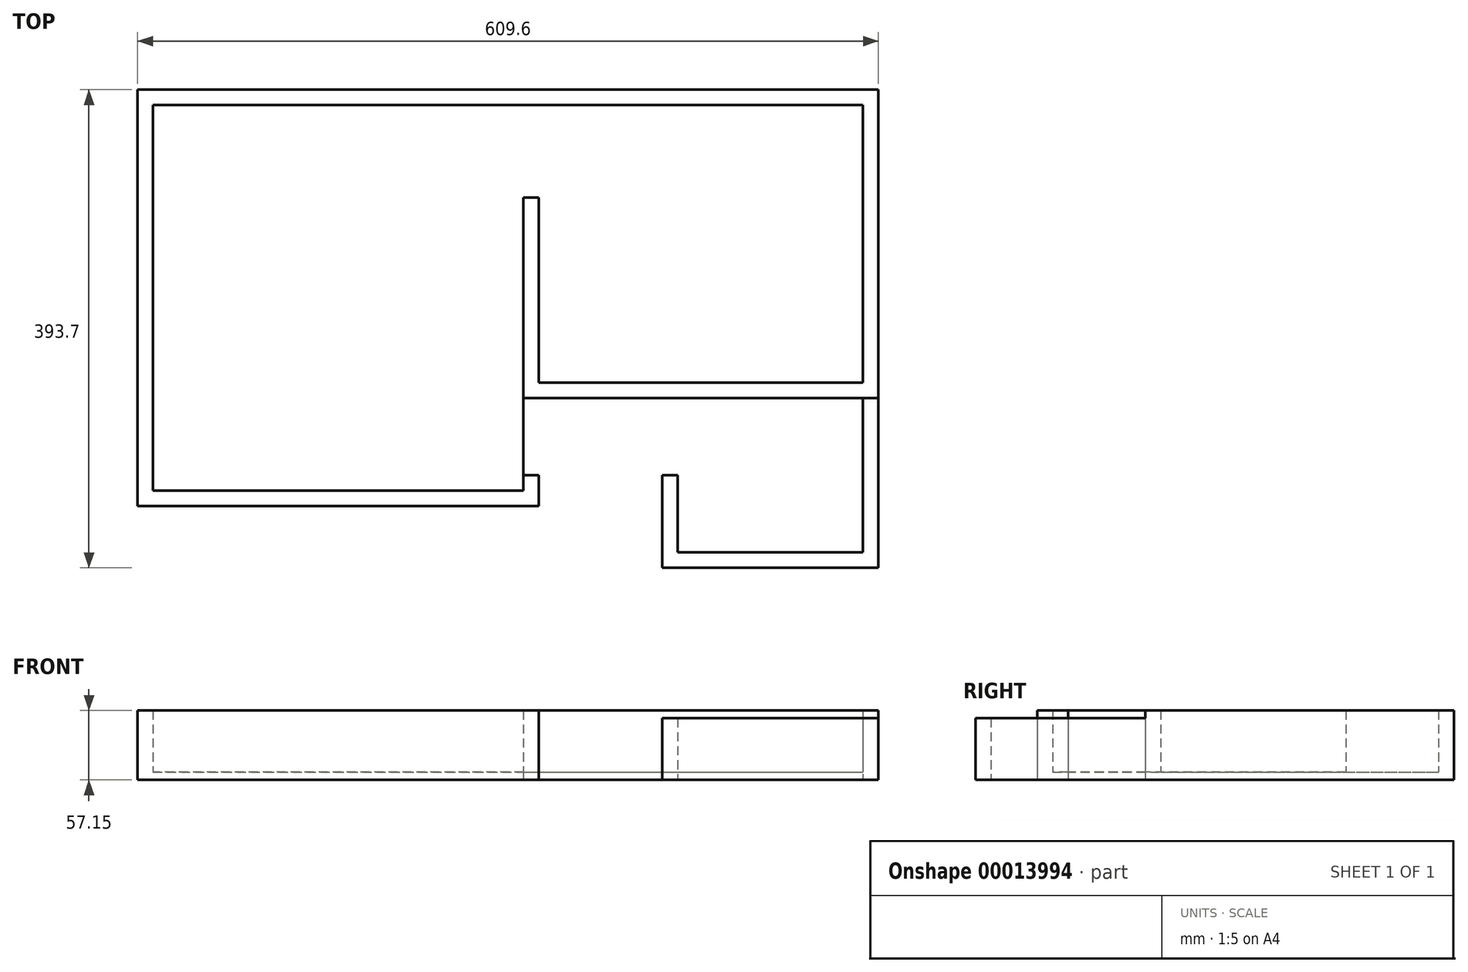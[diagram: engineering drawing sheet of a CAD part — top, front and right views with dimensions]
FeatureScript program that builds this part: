
annotation { "Feature Type Name" : "Feature", "Feature Type Description" : "" }
export const myFeature = defineFeature(function(context is Context, id is Id, definition is map)
    precondition{}
    {
        {
            var Q0;
            Q0=qCreatedBy(makeId("Top.planeOp"),FACE);
            var sketch = newSketch(context, id + "F0", { "sketchPlane" : qUnion([Q0])});
            skLineSegment(sketch, "E0", {"start": v(304.8, 0) * mm, "end": v(0, 0) * mm});
            skLineSegment(sketch, "E1", {"start": v(0, 0) * mm, "end": v(0, 317.5) * mm});
            skLineSegment(sketch, "E2", {"start": v(0, 317.5) * mm, "end": v(584.2, 317.5) * mm});
            skLineSegment(sketch, "E3", {"start": v(304.8, 88.9) * mm, "end": v(304.8, 0) * mm});
            skLineSegment(sketch, "E4", {"start": v(304.8, 88.9) * mm, "end": v(584.2, 88.9) * mm});
            skLineSegment(sketch, "E5", {"start": v(584.2, 88.9) * mm, "end": v(584.2, 317.5) * mm});
            skLineSegment(sketch, "E6.0", {"start": v(-12.7, 330.2) * mm, "end": v(596.9, 330.2) * mm});
            skLineSegment(sketch, "E6.1", {"start": v(-12.7, -12.7) * mm, "end": v(-12.7, 330.2) * mm});
            skLineSegment(sketch, "E6.2", {"start": v(317.5, -12.7) * mm, "end": v(-12.7, -12.7) * mm});
            skLineSegment(sketch, "E7.0", {"start": v(317.5, 76.2) * mm, "end": v(317.5, -12.7) * mm});
            skLineSegment(sketch, "E7.1", {"start": v(317.5, 76.2) * mm, "end": v(596.9, 76.2) * mm});
            skLineSegment(sketch, "E7.2", {"start": v(596.9, 76.2) * mm, "end": v(596.9, 330.2) * mm});
            skSolve(sketch);
        }
        {
            var Q0;
            Q0=makeQuery(id+"F0.imprint","IMPRINT",FACE,{"disambiguationData":[TD([[makeQuery(id+"F0.imprint","IMPRINT",EDGE,{"derivedFrom":sQuery(id+"F0.wireOp",EDGE,"E0")}),1.0]])]});
            extrude(context, id + "F1", {"entities" : qUnion([Q0]), "depth" : 50.8 * mm});
        }
        {
            var Q0;
            Q0=makeQuery(id+"F0.imprint","IMPRINT",FACE,{"disambiguationData":[TD([[makeQuery(id+"F0.imprint","IMPRINT",EDGE,{"derivedFrom":sQuery(id+"F0.wireOp",EDGE,"E0")}),-1.0]])]});
            var Q1;
            Q1=makeQuery(id+"F0.imprint","IMPRINT",FACE,{"disambiguationData":[TD([[makeQuery(id+"F0.imprint","IMPRINT",EDGE,{"derivedFrom":sQuery(id+"F0.wireOp",EDGE,"E0")}),1.0]])]});
            extrude(context, id + "F2", {"entities" : qUnion([Q0, Q1]), "operationType" : NewBodyOperationType.ADD, "oppositeDirection" : true, "depth" : 6.35 * mm});
        }
        {
            var Q0;
            Q0=makeQuery(id+"F2.opExtrude","CAP_FACE",FACE,{"disambiguationData":[OSD([sQuery(id+"F0.wireOp",EDGE,"E6.0"),sQuery(id+"F0.wireOp",EDGE,"E6.1"),sQuery(id+"F0.wireOp",EDGE,"E6.2"),sQuery(id+"F0.wireOp",EDGE,"E7.0"),sQuery(id+"F0.wireOp",EDGE,"E7.1"),sQuery(id+"F0.wireOp",EDGE,"E7.2")])],"isStart":true});
            var sketch = newSketch(context, id + "F3", { "sketchPlane" : qUnion([Q0])});
            skLineSegment(sketch, "E8", {"start": v(304.8, 241.3) * mm, "end": v(304.8, 88.9) * mm});
            skLineSegment(sketch, "E9", {"start": v(304.8, 241.3) * mm, "end": v(317.5, 241.3) * mm});
            skLineSegment(sketch, "E10", {"start": v(317.5, 241.3) * mm, "end": v(317.5, 88.9) * mm});
            skLineSegment(sketch, "E11", {"start": v(317.5, 88.9) * mm, "end": v(304.8, 88.9) * mm});
            skSolve(sketch);
        }
        {
            var Q0;
            Q0=makeQuery(id+"F3.imprint","IMPRINT",FACE,{"disambiguationData":[TD([[makeQuery(id+"F3.imprint","IMPRINT",EDGE,{"derivedFrom":sQuery(id+"F3.wireOp",EDGE,"E8")}),1.0]])]});
            extrude(context, id + "F4", {"entities" : qUnion([Q0]), "operationType" : NewBodyOperationType.ADD, "depth" : 50.8 * mm});
        }
        {
            var Q0;
            {var subQ0=sQuery(id+"F0.wireOp",EDGE,"E7.0");Q0=makeQuery(id+"F2.boolean.opBoolean","MERGE",FACE,{"derivedFrom":[makeQuery(id+"F1.opExtrude","SWEPT_FACE",FACE,{"disambiguationData":[OSD([subQ0])]}),makeQuery(id+"F2.opExtrude","SWEPT_FACE",FACE,{"disambiguationData":[OSD([subQ0])]})]});}
            var sketch = newSketch(context, id + "F5", { "sketchPlane" : qUnion([Q0])});
            skLineSegment(sketch, "E12", {"start": v(12.7, 50.8) * mm, "end": v(12.7, -6.35) * mm});
            skLineSegment(sketch, "E13", {"start": v(12.7, -6.35) * mm, "end": v(76.2, -6.35) * mm});
            skLineSegment(sketch, "E14", {"start": v(76.2, -6.35) * mm, "end": v(76.2, 50.8) * mm});
            skLineSegment(sketch, "E15", {"start": v(76.2, 50.8) * mm, "end": v(12.7, 50.8) * mm});
            skSolve(sketch);
        }
        {
            var Q0;
            Q0=makeQuery(id+"F2.opExtrude","CAP_FACE",FACE,{"disambiguationData":[OSD([sQuery(id+"F0.wireOp",EDGE,"E6.0"),sQuery(id+"F0.wireOp",EDGE,"E6.1"),sQuery(id+"F0.wireOp",EDGE,"E6.2"),sQuery(id+"F0.wireOp",EDGE,"E7.0"),sQuery(id+"F0.wireOp",EDGE,"E7.1"),sQuery(id+"F0.wireOp",EDGE,"E7.2")])],"isStart":false});
            var sketch = newSketch(context, id + "F6", { "sketchPlane" : qUnion([Q0])});
            skLineSegment(sketch, "E16", {"start": v(596.9, -76.2) * mm, "end": v(596.9, 63.5) * mm});
            skLineSegment(sketch, "E17", {"start": v(596.9, 63.5) * mm, "end": v(419.1, 63.5) * mm});
            skLineSegment(sketch, "E18", {"start": v(419.1, 63.5) * mm, "end": v(419.1, -12.7) * mm});
            skLineSegment(sketch, "E19", {"start": v(419.1, -12.7) * mm, "end": v(431.8, -12.7) * mm});
            skLineSegment(sketch, "E20", {"start": v(431.8, -12.7) * mm, "end": v(431.8, 50.8) * mm});
            skLineSegment(sketch, "E21", {"start": v(431.8, 50.8) * mm, "end": v(584.2, 50.8) * mm});
            skLineSegment(sketch, "E22", {"start": v(584.2, 50.8) * mm, "end": v(584.2, -76.2) * mm});
            skLineSegment(sketch, "E23", {"start": v(596.9, -76.2) * mm, "end": v(596.9, -88.9) * mm});
            skLineSegment(sketch, "E24", {"start": v(596.9, -88.9) * mm, "end": v(584.2, -88.9) * mm});
            skLineSegment(sketch, "E25", {"start": v(584.2, -88.9) * mm, "end": v(584.2, -76.2) * mm});
            skSolve(sketch);
        }
        {
            var Q0;
            {var subQ2=sQuery(id+"F6.wireOp",EDGE,"E16");Q0=makeQuery(id+"F6.imprint","IMPRINT",FACE,{"disambiguationData":[TD([[makeQuery(id+"F6.imprint","IMPRINT",EDGE,{"derivedFrom":subQ2}),1.0]])]});}
            extrude(context, id + "F7", {"entities" : qUnion([Q0]), "operationType" : NewBodyOperationType.ADD, "oppositeDirection" : true, "depth" : 50.8 * mm});
        }
        {
            var Q0;
            Q0=makeQuery(id+"F5.imprint","IMPRINT",FACE,{"disambiguationData":[TD([[makeQuery(id+"F5.imprint","IMPRINT",EDGE,{"derivedFrom":sQuery(id+"F5.wireOp",EDGE,"E12")}),1.0]])]});
            extrude(context, id + "F8", {"entities" : qUnion([Q0]), "operationType" : NewBodyOperationType.REMOVE, "oppositeDirection" : true, "depth" : 12.7 * mm});
        }
    });
